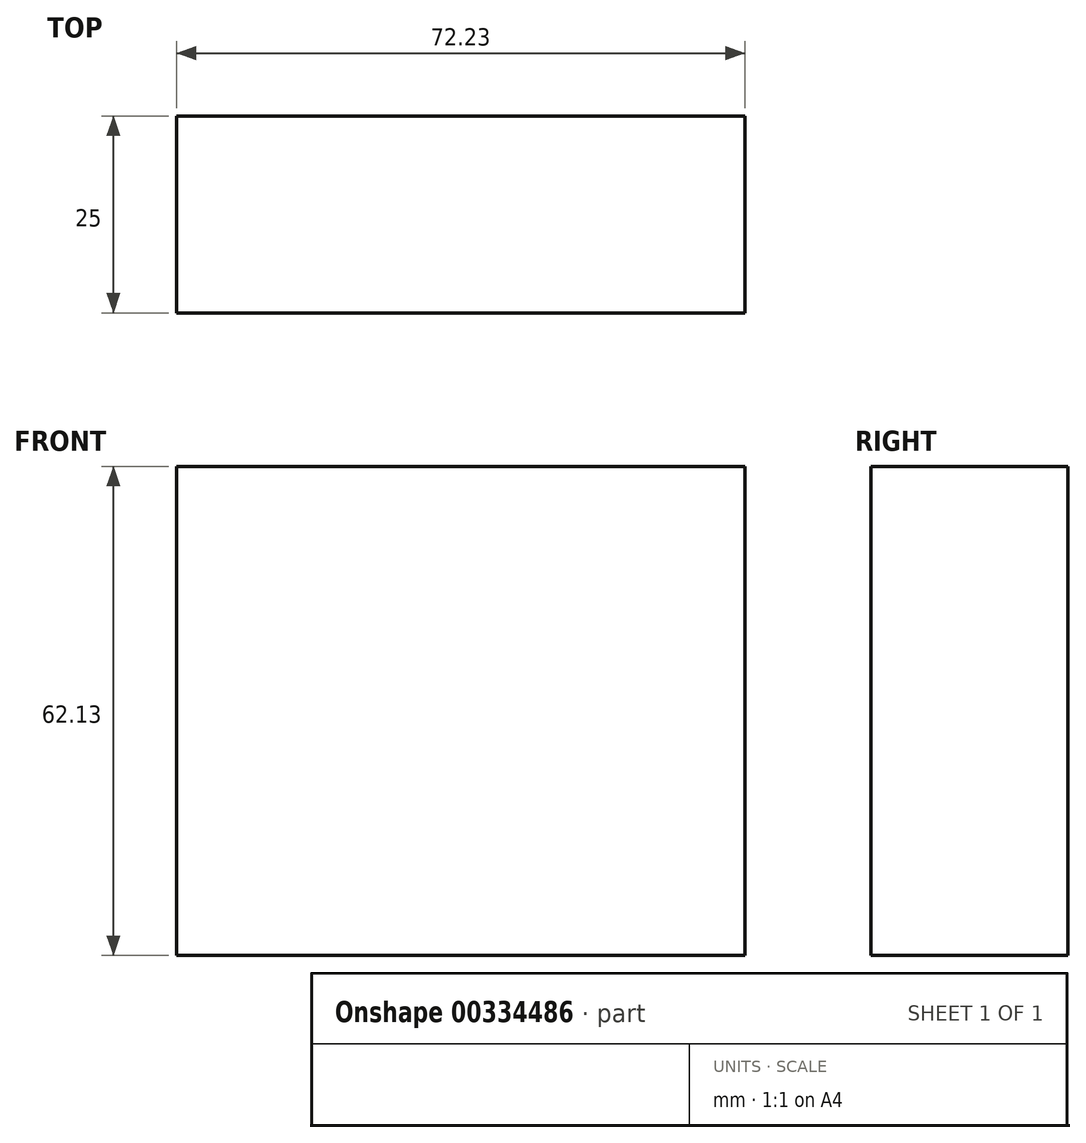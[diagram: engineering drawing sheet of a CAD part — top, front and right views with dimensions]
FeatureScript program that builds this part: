
annotation { "Feature Type Name" : "Feature", "Feature Type Description" : "" }
export const myFeature = defineFeature(function(context is Context, id is Id, definition is map)
    precondition{}
    {
        {
            var Q0;
            Q0=qCreatedBy(makeId("Front.planeOp"),FACE);
            var sketch = newSketch(context, id + "F0", { "sketchPlane" : qUnion([Q0])});
            skLineSegment(sketch, "E0.bottom", {"start": v(-123, -19.17) * mm, "end": v(-50.77, -19.17) * mm});
            skLineSegment(sketch, "E0.top", {"start": v(-123, 42.96) * mm, "end": v(-50.77, 42.96) * mm});
            skLineSegment(sketch, "E0.left", {"start": v(-123, -19.17) * mm, "end": v(-123, 42.96) * mm});
            skLineSegment(sketch, "E0.right", {"start": v(-50.77, -19.17) * mm, "end": v(-50.77, 42.96) * mm});
            skPoint(sketch, "E0.middle", {"position": v(-86.89, 11.9) * mm});
            skSolve(sketch);
        }
        {
            var Q0;
            Q0=makeQuery(id+"F0.imprint","IMPRINT",FACE,{"disambiguationData":[TD([[makeQuery(id+"F0.imprint","IMPRINT",EDGE,{"derivedFrom":sQuery(id+"F0.wireOp",EDGE,"E0.bottom")}),1.0]])]});
            extrude(context, id + "F1", {"entities" : qUnion([Q0]), "depth" : 25 * mm});
        }
    });
